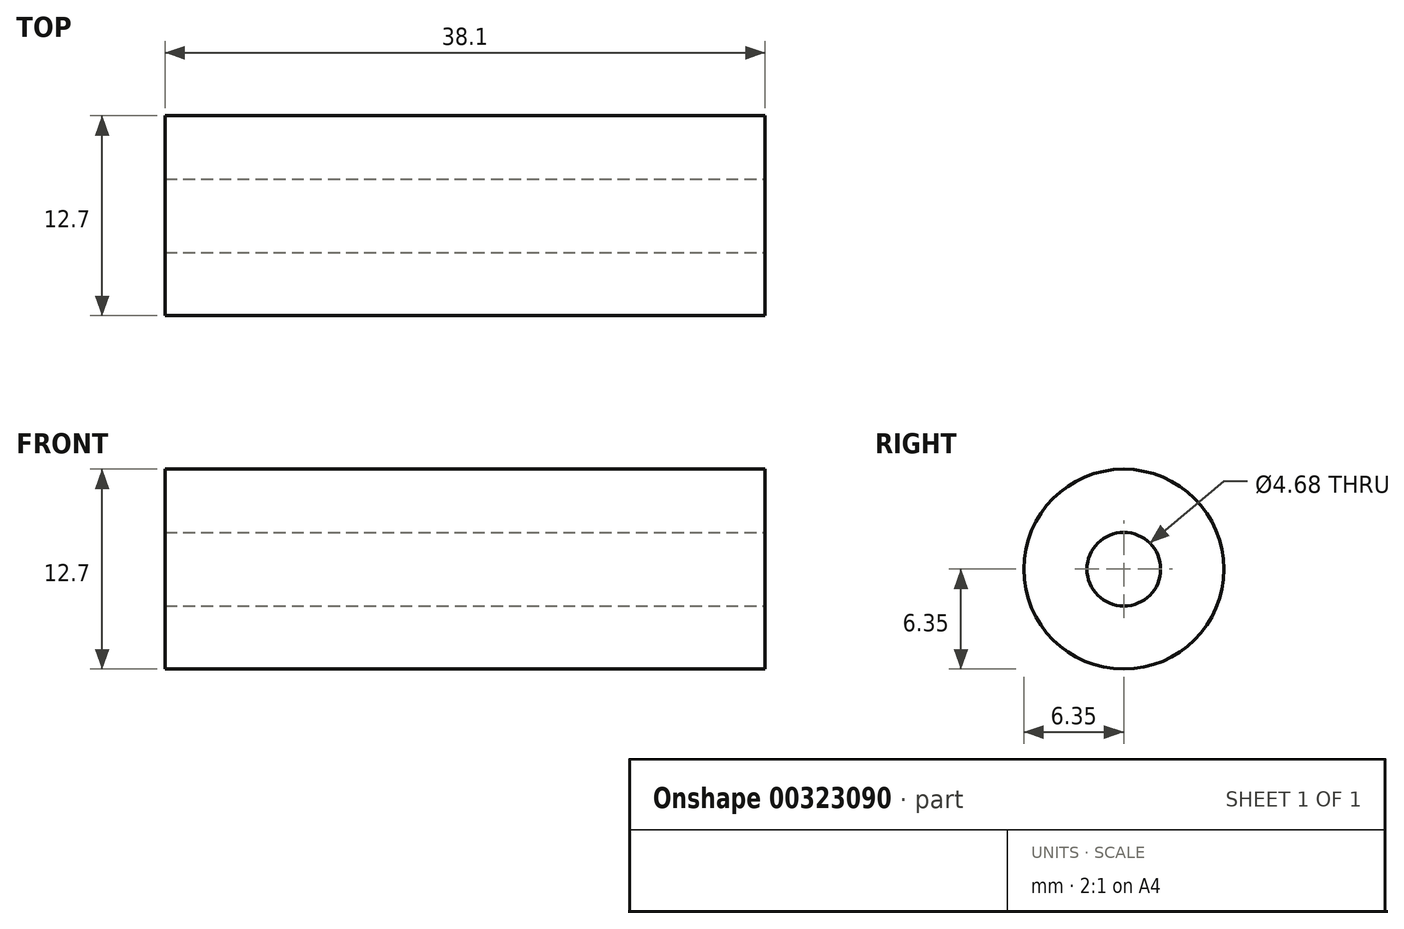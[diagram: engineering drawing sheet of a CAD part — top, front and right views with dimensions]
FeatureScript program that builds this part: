
annotation { "Feature Type Name" : "Feature", "Feature Type Description" : "" }
export const myFeature = defineFeature(function(context is Context, id is Id, definition is map)
    precondition{}
    {
        {
            var Q0;
            Q0=qCreatedBy(makeId("Right.planeOp"),FACE);
            var sketch = newSketch(context, id + "F0", { "sketchPlane" : qUnion([Q0])});
            skCircle(sketch, "E0", {"center": v(0, 0) * mm, "radius": 6.35 * mm});
            skSolve(sketch);
        }
        {
            var Q0;
            Q0 = qSketchRegion(id + "F0", true);
            extrude(context, id + "F1", {"entities" : qUnion([Q0]), "endBound" : BoundingType.SYMMETRIC, "depth" : 38.1 * mm});
        }
        {
            var Q0;
            Q0=makeQuery(id+"F1.opExtrude","CAP_FACE",FACE,{"disambiguationData":[OSD([sQuery(id+"F0.wireOp",EDGE,"E0")])],"isStart":false});
            var sketch = newSketch(context, id + "F2", { "sketchPlane" : qUnion([Q0])});
            skSolve(sketch);
        }
        {
            var Q0;
            Q0=makeQuery(id+"F2.imprint","IMPRINT",FACE,{"disambiguationData":[TD([[makeQuery(id+"F2.imprint","IMPRINT",EDGE,{"derivedFrom":makeQuery(id+"F1.opExtrude","CAP_EDGE",EDGE,{"disambiguationData":[OSD([sQuery(id+"F0.wireOp",EDGE,"E0")])],"isStart":false})}),1.0]])]});
            cPlane(context, id + "F3", {"entities" : qUnion([Q0]), "cplaneType" : CPlaneType.OFFSET, "offset" : 0 * mm, "width" : 152.4 * mm, "height" : 152.4 * mm});
        }
        {
            var Q0;
            Q0=qCreatedBy(id+"F3.planeOp",FACE);
            var sketch = newSketch(context, id + "F4", { "sketchPlane" : qUnion([Q0])});
            skCircle(sketch, "E1", {"center": v(0, 0) * mm, "radius": 2.34 * mm});
            skSolve(sketch);
        }
        {
            var Q0;
            Q0 = qSketchRegion(id + "F4", true);
            var Q1;
            Q1=makeQuery(id+"F1.opExtrude","CAP_FACE",FACE,{"disambiguationData":[OSD([sQuery(id+"F0.wireOp",EDGE,"E0")])],"isStart":true});
            extrude(context, id + "F5", {"entities" : qUnion([Q0, Q1]), "operationType" : NewBodyOperationType.REMOVE, "oppositeDirection" : true, "depth" : 50.3 * mm});
        }
    });
